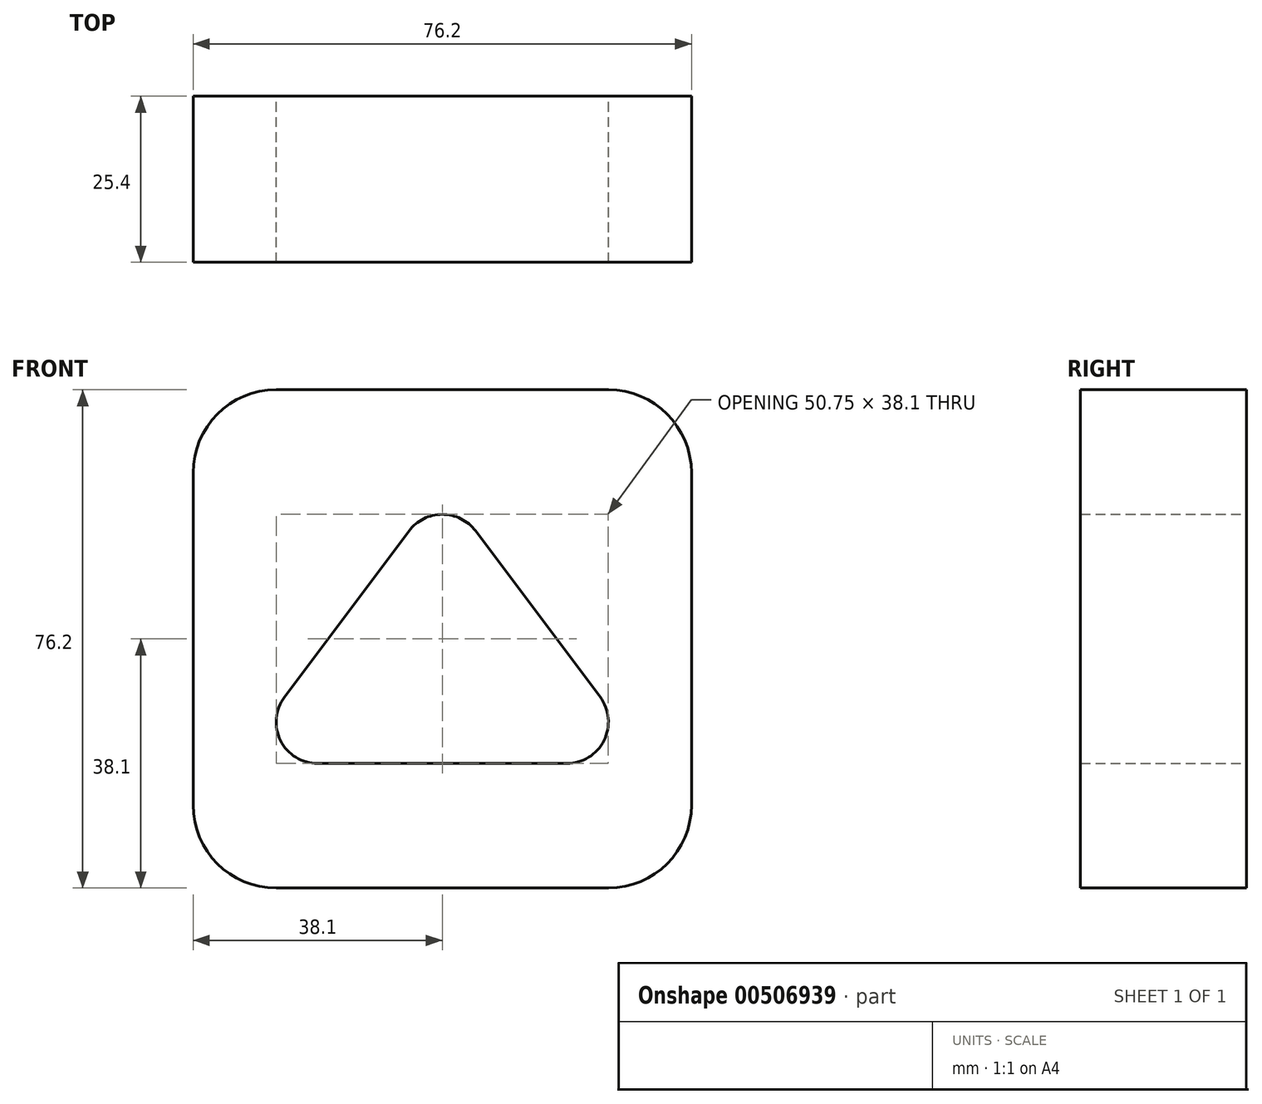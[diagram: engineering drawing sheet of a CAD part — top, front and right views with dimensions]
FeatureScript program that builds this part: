
annotation { "Feature Type Name" : "Feature", "Feature Type Description" : "" }
export const myFeature = defineFeature(function(context is Context, id is Id, definition is map)
    precondition{}
    {
        {
            var Q0;
            Q0=qCreatedBy(makeId("Front.planeOp"),FACE);
            var sketch = newSketch(context, id + "F0", { "sketchPlane" : qUnion([Q0])});
            skLineSegment(sketch, "E0", {"start": v(12.7, 0) * mm, "end": v(63.5, 0) * mm});
            skLineSegment(sketch, "E1", {"start": v(76.2, 12.7) * mm, "end": v(76.2, 63.5) * mm});
            skLineSegment(sketch, "E2", {"start": v(63.5, 76.2) * mm, "end": v(12.7, 76.2) * mm});
            skLineSegment(sketch, "E3", {"start": v(0, 63.5) * mm, "end": v(0, 12.7) * mm});
            skArc(sketch, "E4", {"start": v(13.97, 29.21) * mm, "mid": v(13.37, 22.56) * mm, "end": v(19.05, 19.05) * mm});
            skArc(sketch, "E5", {"start": v(57.15, 19.05) * mm, "mid": v(62.83, 22.56) * mm, "end": v(62.23, 29.2) * mm});
            skArc(sketch, "E6", {"start": v(43.18, 54.6) * mm, "mid": v(38.1, 57.15) * mm, "end": v(33.02, 54.6) * mm});
            skLineSegment(sketch, "E7", {"start": v(13.97, 29.21) * mm, "end": v(33.02, 54.6) * mm});
            skLineSegment(sketch, "E8", {"start": v(43.18, 54.6) * mm, "end": v(62.23, 29.21) * mm});
            skLineSegment(sketch, "E9", {"start": v(19.05, 19.05) * mm, "end": v(57.15, 19.05) * mm});
            skPoint(sketch, "E10.visualSharp", {"position": v(0, 76.2) * mm});
            skArc(sketch, "E10.filletArc", {"start": v(12.7, 76.2) * mm, "mid": v(3.72, 72.48) * mm, "end": v(0, 63.5) * mm});
            skPoint(sketch, "E11.visualSharp", {"position": v(76.2, 76.2) * mm});
            skArc(sketch, "E11.filletArc", {"start": v(76.2, 63.5) * mm, "mid": v(72.48, 72.48) * mm, "end": v(63.5, 76.2) * mm});
            skPoint(sketch, "E12.visualSharp", {"position": v(0, 0) * mm});
            skArc(sketch, "E12.filletArc", {"start": v(0, 12.7) * mm, "mid": v(3.72, 3.72) * mm, "end": v(12.7, 0) * mm});
            skPoint(sketch, "E13.visualSharp", {"position": v(76.2, 0) * mm});
            skArc(sketch, "E13.filletArc", {"start": v(63.5, 0) * mm, "mid": v(72.48, 3.72) * mm, "end": v(76.2, 12.7) * mm});
            skSolve(sketch);
        }
        {
            var Q0;
            Q0=makeQuery(id+"F0.imprint","IMPRINT",FACE,{"disambiguationData":[TD([[makeQuery(id+"F0.imprint","IMPRINT",EDGE,{"derivedFrom":sQuery(id+"F0.wireOp",EDGE,"E0")}),1.0]])]});
            extrude(context, id + "F1", {"entities" : qUnion([Q0]), "depth" : 25.4 * mm});
        }
    });
